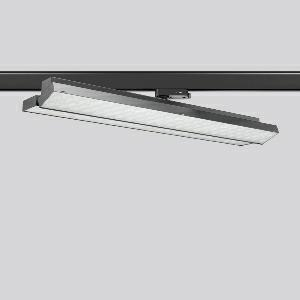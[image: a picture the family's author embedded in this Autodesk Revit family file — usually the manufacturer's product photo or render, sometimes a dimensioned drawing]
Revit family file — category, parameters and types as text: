
# Revit family: tx-move_742161_003_2_76_9584
name_source: partatom
category: Lighting Fixtures
units: mm (PartAtom-declared; Revit-internal decimal feet)

## family parameters
Cut with Voids When Loaded = No
Host = Face
Light Source = No
Part Type = Normal
Room Calculation Point = No
Round Connector Dimension = Use Diameter
Shared = No

## types (1)
- MultiLumen 1 (1 x LED Modul 927, 2100 lm, 2700)
    Apparent Load = 38 VA
    CIE Flux Codes = 90 97 99 100 100
    Color Rendering = 92
    Color Temperature = 2700
    Default Elevation = 1800 mm
    Description = Series: TX-MOVE
Multifunctional surface-mounted spotlight for area lighting. Very flat design. Housing: sheet steel, powder-coated. Rotation range: 356°. Swivel range: 90°. Consistent alignment possible with visible tilt scale. High-efficiency LED units with optimum light control thanks to clear plastic (PC) lens optics. Spezielle Mikrostrukturen reduzieren Gelbsaum. Symmetrical light distribution. Best colour rendering with CRI >90 for fresh products and coloured textiles. With adapter for RZB 3-circuit DALI tracks. Suitable for Track on ceiling. MultiLumen: Luminous flux adjustable in 3 steps. Factory setting is the highest luminous flux. Environmentally friendly and resource-saving due to replaceable and recyclable components. Very good glare control, ideal for till areas. 
Colour: deep black, matt (RAL 9005)
Length: 570 mm
Width: 119 mm
Height: 88 mm
Lamp: LED
Socket: without socket
Colour temperature: 2700K
Colour rendering index (CRI): 90
System power: 38 W
Rated luminous flux: 4200 lm
Luminous efficiency: 111 lm/W
System power 2: 51 W
Rated luminous flux 2: 5500 lm
Luminous efficiency 2: 108 lm/W
System power 3: 62 W
Rated luminous flux 3: 6500 lm
Luminous efficiency 3: 105 lm/W
Control gear: Dimmable EVG, DALI
Protection class: I
Type of protection: IP 20
    Height = 75 mm
    Lamp = 1 x LED Modul 927
    Lamp Light Flux = 2100 lm
    Lamp count = 1
    Length = 569 mm
    Lifetime = 50000 h
    Luminous efficacy = 111 lm/W
    Manufacturer = RZB
    ModVariant = No
    Model = 742161.003.2.76
    Mounting Place = Ceiling
    Mounting Type = Surface mounted
    Number of Poles = 1
    OnlyDefault = Yes
    Power Factor = 1
    Product Name = TX-MOVE
    Product group = Track mounted projectors
    ProductGroupID = 301
    Protection Class = Protection class I
    Protection Degree = IP 20
    RLX_Detail_Level = 1
    RLX_Emergency_Light_Flux = 0 lm
    RLX_Emergency_Type = 0
    RLX_Emergency_Type_DB = No
    RlxData = <blob elided: 37053 chars, md5=fc1871c5>
    Socket = socket
    Standby Power = 0 W
    System Light Flux = 4200 lm
    System Power = 38 W
    Type Comments = MultiLumen 1
    Type Image = 742162.003.jpg
    URL = http://relux.com
    VarID = multilumen_1
    Voltage = 0 V
    Weight = 0.00 kg
    Width = 119 mm

## geometry (parser evidence)
native form markers: Blend x4, Sweep x13
no freeform markers — native parametric forms only
